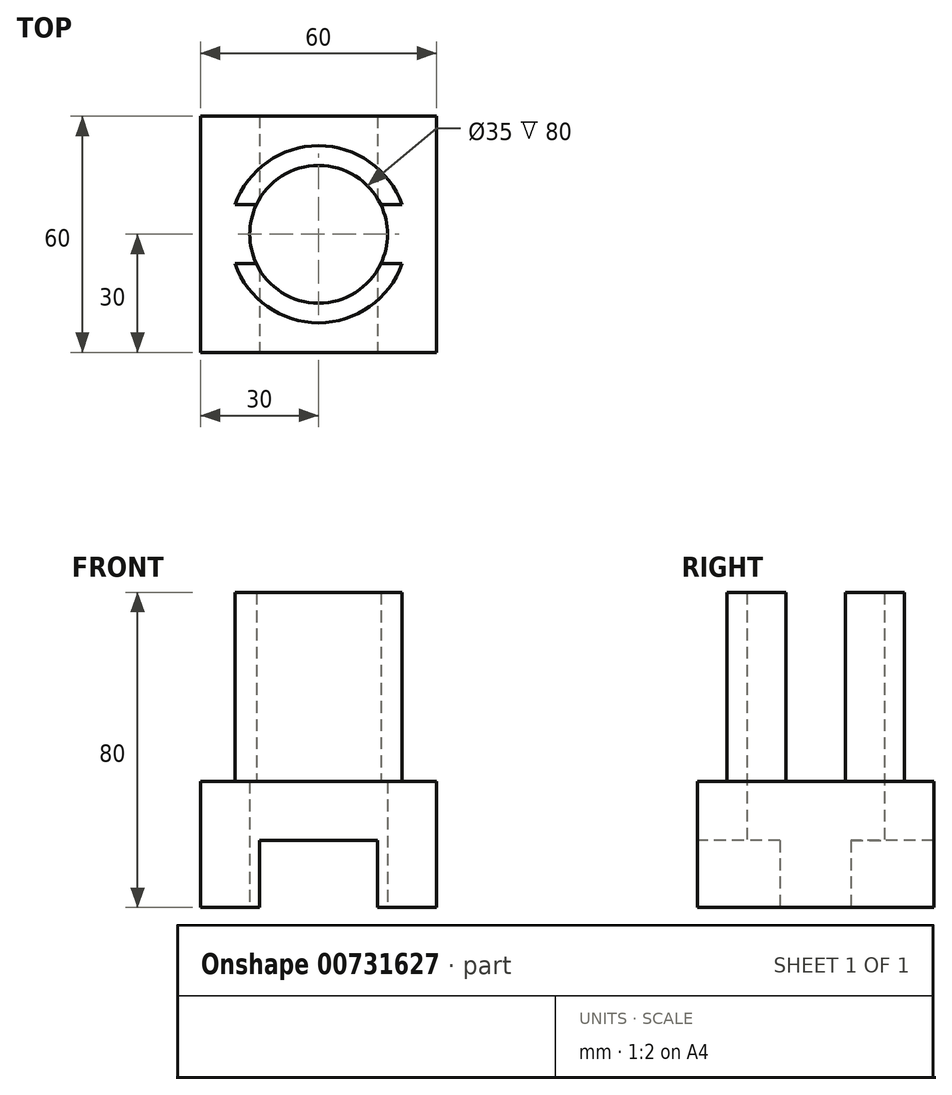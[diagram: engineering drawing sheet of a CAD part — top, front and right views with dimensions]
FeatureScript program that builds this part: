
annotation { "Feature Type Name" : "Feature", "Feature Type Description" : "" }
export const myFeature = defineFeature(function(context is Context, id is Id, definition is map)
    precondition{}
    {
        {
            var Q0;
            Q0=qCreatedBy(makeId("Top.planeOp"),FACE);
            var sketch = newSketch(context, id + "F0", { "sketchPlane" : qUnion([Q0])});
            skLineSegment(sketch, "E0.bottom", {"start": v(-30, 30) * mm, "end": v(30, 30) * mm});
            skLineSegment(sketch, "E0.top", {"start": v(-30, -30) * mm, "end": v(30, -30) * mm});
            skLineSegment(sketch, "E0.left", {"start": v(-30, 30) * mm, "end": v(-30, -30) * mm});
            skLineSegment(sketch, "E0.right", {"start": v(30, 30) * mm, "end": v(30, -30) * mm});
            skSolve(sketch);
        }
        {
            var Q0;
            Q0=makeQuery(id+"F0.imprint","IMPRINT",FACE,{"disambiguationData":[TD([[makeQuery(id+"F0.imprint","IMPRINT",EDGE,{"derivedFrom":sQuery(id+"F0.wireOp",EDGE,"E0.bottom")}),-1.0]])]});
            extrude(context, id + "F1", {"entities" : qUnion([Q0]), "depth" : 32 * mm, "offsetDistance" : 25 * mm});
        }
        {
            var Q0;
            Q0=makeQuery(id+"F1.opExtrude","CAP_FACE",FACE,{"disambiguationData":[OSD([sQuery(id+"F0.wireOp",EDGE,"E0.bottom"),sQuery(id+"F0.wireOp",EDGE,"E0.top"),sQuery(id+"F0.wireOp",EDGE,"E0.left"),sQuery(id+"F0.wireOp",EDGE,"E0.right")])],"isStart":false});
            var sketch = newSketch(context, id + "F2", { "sketchPlane" : qUnion([Q0])});
            skArc(sketch, "E1", {"start": v(21.21, 7.5) * mm, "mid": v(0, 22.5) * mm, "end": v(-21.21, 7.5) * mm});
            skArc(sketch, "E2", {"start": v(15.81, 7.5) * mm, "mid": v(0, 17.5) * mm, "end": v(-15.81, 7.5) * mm});
            skLineSegment(sketch, "E3", {"start": v(-15.81, 7.5) * mm, "end": v(-21.21, 7.5) * mm});
            skLineSegment(sketch, "E4", {"start": v(15.81, 7.5) * mm, "end": v(21.21, 7.5) * mm});
            skLineSegment(sketch, "E5", {"start": v(-15.81, -7.5) * mm, "end": v(-21.21, -7.5) * mm});
            skLineSegment(sketch, "E6", {"start": v(15.81, -7.5) * mm, "end": v(21.21, -7.5) * mm});
            skPoint(sketch, "E7.orphan", {"position": v(-12.6, 7.5) * mm});
            skPoint(sketch, "E8.orphan", {"position": v(10.54, 7.5) * mm});
            skArc(sketch, "E9.trimOffspring", {"start": v(-15.81, -7.5) * mm, "mid": v(0, -17.5) * mm, "end": v(15.81, -7.5) * mm});
            skArc(sketch, "E10.trimOffspring", {"start": v(-21.21, -7.5) * mm, "mid": v(0, -22.5) * mm, "end": v(21.21, -7.5) * mm});
            skSolve(sketch);
        }
        {
            var Q0;
            Q0 = qSketchRegion(id + "F2", true);
            extrude(context, id + "F3", {"entities" : qUnion([Q0]), "operationType" : NewBodyOperationType.ADD, "depth" : 48 * mm, "offsetDistance" : 25 * mm});
        }
        {
            var Q0;
            Q0=makeQuery(id+"F1.opExtrude","CAP_FACE",FACE,{"disambiguationData":[OSD([sQuery(id+"F0.wireOp",EDGE,"E0.bottom"),sQuery(id+"F0.wireOp",EDGE,"E0.top"),sQuery(id+"F0.wireOp",EDGE,"E0.left"),sQuery(id+"F0.wireOp",EDGE,"E0.right")])],"isStart":false});
            var sketch = newSketch(context, id + "F4", { "sketchPlane" : qUnion([Q0])});
            skCircle(sketch, "E11", {"center": v(0, 0) * mm, "radius": 17.5 * mm});
            skSolve(sketch);
        }
        {
            var Q0;
            {var subQ0=sQuery(id+"F4.wireOp",EDGE,"E11");var subQ1=makeQuery(id+"F4.imprint","INTERSECT",VERTEX,{"derivedFrom":[makeQuery(id+"F3.opExtrude","CAP_EDGE",EDGE,{"disambiguationData":[OSD([sQuery(id+"F2.wireOp",EDGE,"E5")])],"isStart":true}),subQ0]});Q0=makeQuery(id+"F4.imprint","IMPRINT",FACE,{"disambiguationData":[TD([[makeQuery(id+"F4.imprint","IMPRINT",EDGE,{"disambiguationData":[TD([[subQ1,-1.0]])],"derivedFrom":subQ0}),1.0]])]});}
            extrude(context, id + "F5", {"entities" : qUnion([Q0]), "operationType" : NewBodyOperationType.REMOVE, "oppositeDirection" : true, "depth" : 32 * mm, "offsetDistance" : 25 * mm});
        }
        {
            var Q0;
            Q0=makeQuery(id+"F1.opExtrude","SWEPT_FACE",FACE,{"disambiguationData":[OSD([sQuery(id+"F0.wireOp",EDGE,"E0.top")])]});
            var sketch = newSketch(context, id + "F6", { "sketchPlane" : qUnion([Q0])});
            skLineSegment(sketch, "E12.bottom", {"start": v(-15, 17) * mm, "end": v(15, 17) * mm});
            skLineSegment(sketch, "E12.top", {"start": v(-15, 0) * mm, "end": v(15, 0) * mm});
            skLineSegment(sketch, "E12.left", {"start": v(-15, 17) * mm, "end": v(-15, 0) * mm});
            skLineSegment(sketch, "E12.right", {"start": v(15, 17) * mm, "end": v(15, 0) * mm});
            skSolve(sketch);
        }
        {
            var Q0;
            Q0 = qSketchRegion(id + "F6", true);
            extrude(context, id + "F7", {"entities" : qUnion([Q0]), "operationType" : NewBodyOperationType.REMOVE, "oppositeDirection" : true, "depth" : 60 * mm, "offsetDistance" : 25 * mm});
        }
    });
